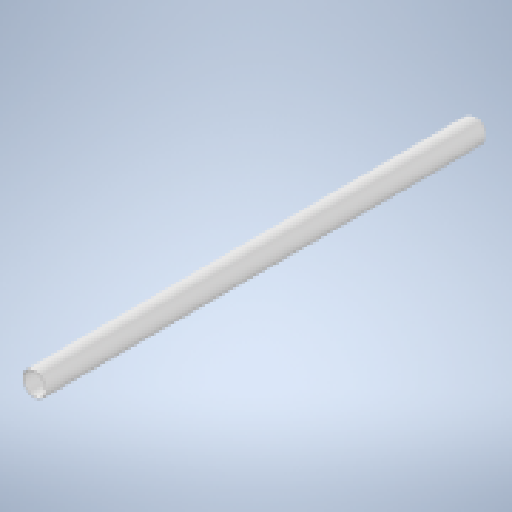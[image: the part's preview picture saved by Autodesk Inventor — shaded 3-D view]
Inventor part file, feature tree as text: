
AUTODESK INVENTOR PART (.ipt)
format: ipt  version: 2024.2 (Build 282272000, 272)  size: 174,080 bytes
history: native  units: in
note: dims shown in document units (in); Inventor stores cm internally (conversion verified against a paired STEP export)
features: extrude x3, chamfer x1, sketch x1
ambient origin geometry x8: Origin, YZ Plane, XZ Plane, XY Plane, X Axis, Y Axis, Z Axis, Center Point
bodies: Solid1 (feature_tree)
feature tree (5):
  extrude  "Extrusion1"  Depth=0.3937in
  extrude  "Extrusion6"  Depth=7.0866in TaperAngle=0.0deg
  extrude  "Extrusion7"  Depth=0.3937in TaperAngle=0.0deg
  chamfer  "Chamfer1"  Distance=0.378in
  sketch  "Sketch7"  dims[d0=0.3638in d1=0.3937in d3=7.0866in d4=0.0in d21=0.3937in d22=0.0in d23=0.378in d24=0.2362in d25=0.0in d26=0.0591in d27=0.0787in d28=45.0deg]
